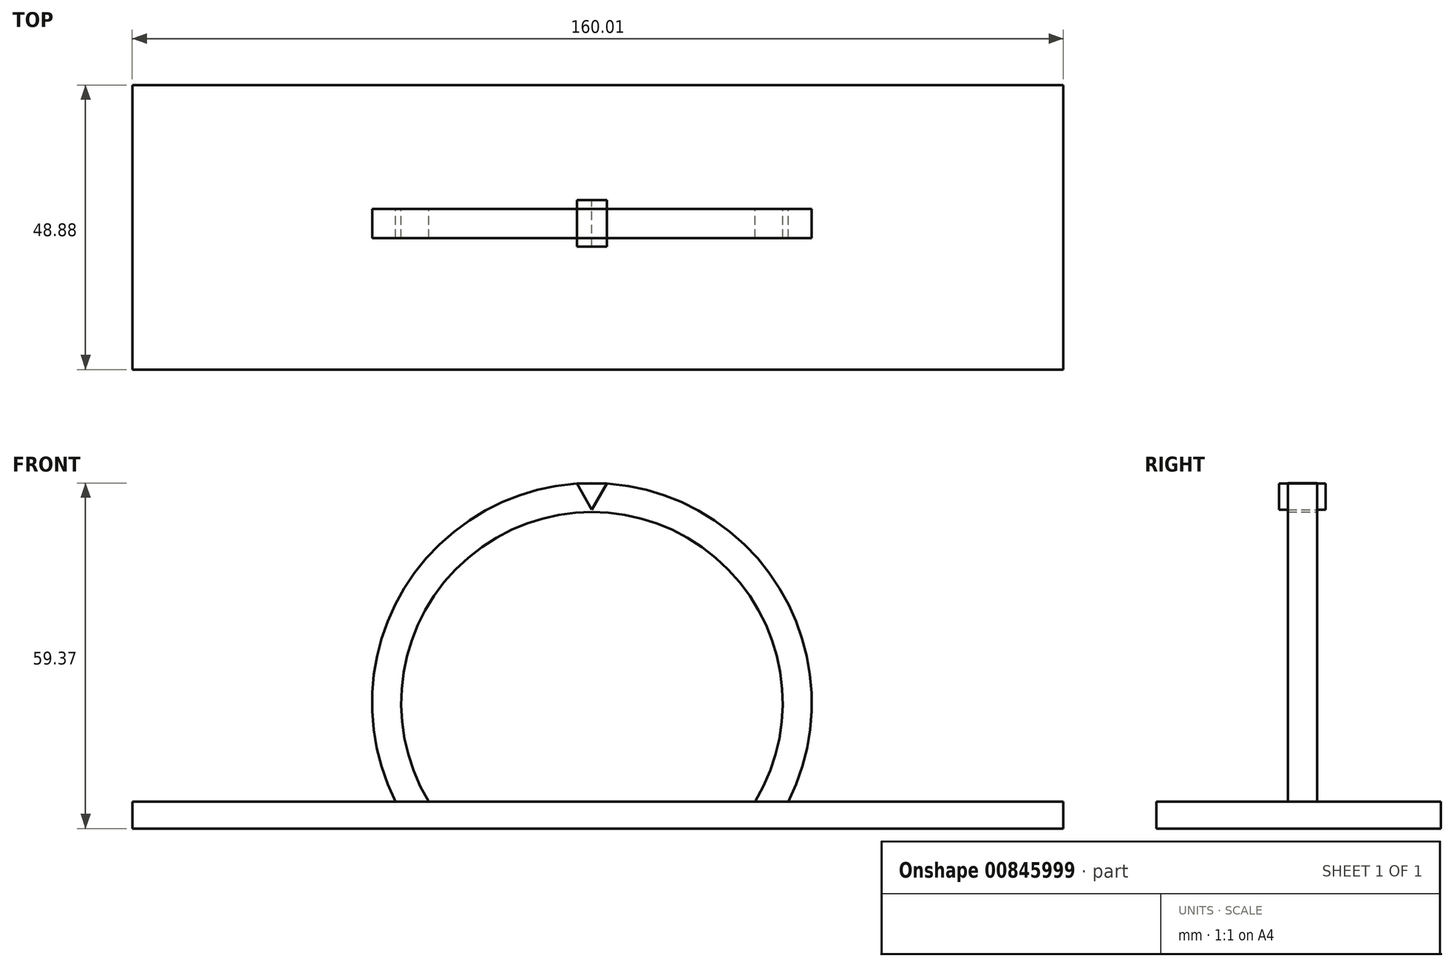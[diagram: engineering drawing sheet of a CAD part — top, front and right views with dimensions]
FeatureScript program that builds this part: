
annotation { "Feature Type Name" : "Feature", "Feature Type Description" : "" }
export const myFeature = defineFeature(function(context is Context, id is Id, definition is map)
    precondition{}
    {
        {
            var Q0;
            Q0=qCreatedBy(makeId("Top.planeOp"),FACE);
            var sketch = newSketch(context, id + "F0", { "sketchPlane" : qUnion([Q0])});
            skLineSegment(sketch, "E0.bottom", {"start": v(-81.99, 23.8) * mm, "end": v(78.02, 23.8) * mm});
            skLineSegment(sketch, "E0.top", {"start": v(-81.99, -25.09) * mm, "end": v(78.02, -25.09) * mm});
            skLineSegment(sketch, "E0.left", {"start": v(-81.99, 23.8) * mm, "end": v(-81.99, -25.09) * mm});
            skLineSegment(sketch, "E0.right", {"start": v(78.02, 23.8) * mm, "end": v(78.02, -25.09) * mm});
            skSolve(sketch);
        }
        {
            var Q0;
            Q0=makeQuery(id+"F0.imprint","IMPRINT",FACE,{"disambiguationData":[TD([[makeQuery(id+"F0.imprint","IMPRINT",EDGE,{"derivedFrom":sQuery(id+"F0.wireOp",EDGE,"E0.bottom")}),-1.0]])]});
            extrude(context, id + "F1", {"entities" : qUnion([Q0]), "depth" : 4.6 * mm, "offsetDistance" : 25 * mm});
        }
        {
            var Q0;
            Q0=qCreatedBy(makeId("Front.planeOp"),FACE);
            var sketch = newSketch(context, id + "F2", { "sketchPlane" : qUnion([Q0])});
            skArc(sketch, "E1", {"start": v(28.73, 1.1) * mm, "mid": v(-3, 59.37) * mm, "end": v(-34.73, 1.1) * mm});
            skArc(sketch, "E2.0", {"start": v(24.53, 3.81) * mm, "mid": v(-3, 54.37) * mm, "end": v(-30.53, 3.81) * mm});
            skLineSegment(sketch, "E3", {"start": v(-34.73, 1.1) * mm, "end": v(-30.53, 3.81) * mm});
            skLineSegment(sketch, "E4", {"start": v(28.73, 1.1) * mm, "end": v(24.53, 3.81) * mm});
            skSolve(sketch);
        }
        {
            var Q0;
            Q0=makeQuery(id+"F2.imprint","IMPRINT",FACE,{"disambiguationData":[TD([[makeQuery(id+"F2.imprint","IMPRINT",EDGE,{"derivedFrom":sQuery(id+"F2.wireOp",EDGE,"E1")}),1.0]])]});
            extrude(context, id + "F3", {"entities" : qUnion([Q0]), "operationType" : NewBodyOperationType.ADD, "endBound" : BoundingType.SYMMETRIC, "depth" : 5 * mm, "offsetDistance" : 25 * mm});
        }
        {
            var Q0;
            Q0=makeQuery(id+"F3.opExtrude","CAP_FACE",FACE,{"disambiguationData":[OSD([sQuery(id+"F2.wireOp",EDGE,"E1"),sQuery(id+"F2.wireOp",EDGE,"E2.0"),sQuery(id+"F2.wireOp",EDGE,"E3"),sQuery(id+"F2.wireOp",EDGE,"E4")])],"isStart":false});
            var sketch = newSketch(context, id + "F4", { "sketchPlane" : qUnion([Q0])});
            skCircle(sketch, "E5.cCircle", {"center": v(-3, 57.78) * mm, "radius": 1.5 * mm, "construction": true});
            skLineSegment(sketch, "E5.0", {"start": v(-5.6, 59.28) * mm, "end": v(-0.4, 59.28) * mm});
            skLineSegment(sketch, "E5.1", {"start": v(-0.4, 59.28) * mm, "end": v(-3, 54.78) * mm});
            skLineSegment(sketch, "E5.2", {"start": v(-3, 54.78) * mm, "end": v(-5.6, 59.28) * mm});
            skPoint(sketch, "E5.0.midPoint", {"position": v(-3, 57.87) * mm});
            skSolve(sketch);
        }
        {
            var Q0;
            Q0=makeQuery(id+"F4.imprint","IMPRINT",FACE,{"disambiguationData":[TD([[makeQuery(id+"F4.imprint","IMPRINT",EDGE,{"derivedFrom":sQuery(id+"F4.wireOp",EDGE,"E5.0")}),-1.0]])]});
            extrude(context, id + "F5", {"entities" : qUnion([Q0]), "endBound" : BoundingType.SYMMETRIC, "depth" : 8 * mm, "offsetDistance" : 25 * mm});
        }
        {
            var Q0;
            Q0=makeQuery(id+"F5.opExtrude","SWEPT_BODY",BODY,{"disambiguationData":[OSD([sQuery(id+"F4.wireOp",EDGE,"E5.0"),sQuery(id+"F4.wireOp",EDGE,"E5.1"),sQuery(id+"F4.wireOp",EDGE,"E5.2")])]});
            var Q1;
            Q1=makeQuery(id+"F1.opExtrude","CAP_EDGE",EDGE,{"disambiguationData":[OSD([sQuery(id+"F0.wireOp",EDGE,"E0.right")])],"isStart":false});
            transform(context, id + "F6", {"entities" : qUnion([Q0]), "transformType" : TransformType.TRANSLATION_DISTANCE, "transformDirection" : qUnion([Q1]), "distance" : 2.5 * mm, "oppositeDirection" : true, "makeCopy" : false});
        }
    });
